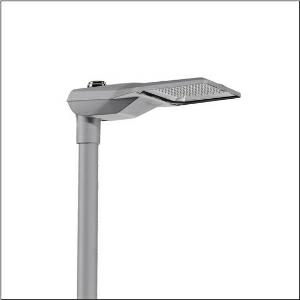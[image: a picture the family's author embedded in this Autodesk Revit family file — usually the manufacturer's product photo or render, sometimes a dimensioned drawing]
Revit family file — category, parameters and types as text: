
# Revit family: streetlight_sl_21_midi___st0_8a_5xe7c47n08nb_23c8
name_source: partatom
category: Lighting Fixtures
units: mm (PartAtom-declared; Revit-internal decimal feet)

## family parameters
Cut with Voids When Loaded = No
Host = Face
Light Source = No
Part Type = Normal
Room Calculation Point = No
Round Connector Dimension = Use Diameter
Shared = No

## types (1)
- --- (1 x LED, 23710 lm, 151.2 W, 4000K)
    Apparent Load = 151 VA
    CIE Flux Codes = 41 75 97 100 100
    Color Rendering = 70
    Color Temperature = 4000K
    Default Elevation = 1800 mm
    Description = Streetlight SL 21 midi, mast luminaire, primary light control with lens, of PMMA, primary optical cover: cover, of toughened safety glass, transparent, light distribution: ST0.8a, light emission: direct distribution, primary light characteristic: asymmetric, installation type: side-entry, LED, 3G 2.5mm², High Power LED, rated luminous flux: 23.710lm, luminous efficacy: 157lm/W, light colour: 740, colour temperature: 4000K, control gear: NEMA (7pin), control: overheat protection, pre-setting: linear dimming characteristic, constant luminous flux control, time-dependent luminous flux control, flexible luminous flux parameterisation, mains connection: 220..240V, AC, 50/60Hz, connection cable pre-assembled, cable length: 12,5m, wiring characteristics: H05VV-F, start of lifetime: 151W, end of service life: 157W, reduction: 70W, luminaire housing, of diecast aluminium (EN AC-44300), powder-coated, Siteco® metallic grey (DB 702S), corrosivity category C5 mid according to DIN EN ISO 12944, multi-level sealing system, sealing non-destructively replaceable, inclination adjustable: 0°, 5°, 10°, 15°, length: 644mm, width: 335mm, height: 110mm, spigot size: 42mm (side-entry), mounting height: 4..8m, protection rating (complete): IP66, insulation class (complete): insulation class I (protective earthing), certification: CE, ENEC, ENEC+, VDE, impact resistance: IK10, permissible operating ambient temperature for outdoor applications: -40..+50°C, standard-compliant lighting for roads and squares, packaging unit: 1 piece

Light Distribution: ST0.8a
    Height = 111 mm
    Lamp = 1 x LED
    Lamp Light Flux = 23710 lm
    Lamp Power = 151.2 W
    Lamp count = 1
    Length = 644 mm
    Luminous efficacy = 157 lm/W
    Manufacturer = Siteco
    ModVariant = No
    Model = 5XE7C47N08NB
    Number of Poles = 1
    OnlyDefault = Yes
    Power Factor = 1
    Product Name = Streetlight SL 21 midi | ST0.8a
    Product group = mast luminaire | pylon top
    ProductGroupID = 6100
    Protection Class = Protection class I
    Protection Degree = IP 66
    RLX_Detail_Level = 1
    RLX_Emergency_Light_Flux = 0 lm
    RLX_Emergency_Type = 0
    RLX_Emergency_Type_DB = No
    RlxData = <blob elided: 26641 chars, md5=8e20b96a>
    Socket = socket
    Standby Power = 0 W
    System Light Flux = 23710 lm
    System Power = 151 W
    Type Comments = factory setting: luminous flux: 100 % | dim-lin: 254 | 802 mA
    Type Image = l_1294377.jpg
    URL = http://relux.com
    VarID = @adj_155315
    Voltage = 0 V
    Weight = 0.00 kg
    Width = 336 mm

## geometry (parser evidence)
native form markers: Blend x4, Sweep x9
no freeform markers — native parametric forms only
